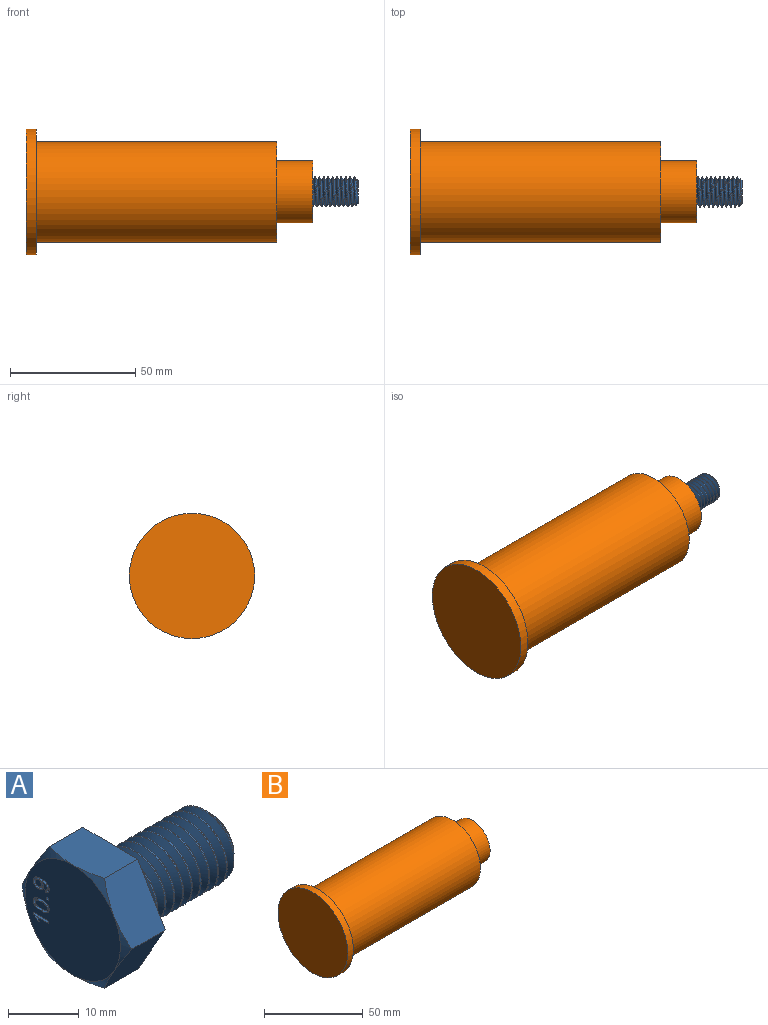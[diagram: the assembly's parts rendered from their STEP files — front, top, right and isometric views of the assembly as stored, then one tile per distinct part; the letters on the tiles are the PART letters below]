
ASSEMBLY  parts=2 mates=1
PART A: 61 faces, bbox 28.9x22.8x22.8 mm
  f0: plane 19x19mm, normal (-1,0,0), area 272.6mm2, adj f14,f15,f16,f17,f18,f19,f20,f21
  f1: plane 11.88x8.41mm, normal (0,0,-1), area 79.1mm2, adj f2,f6,f13,f16,f17
  f2: plane 10.4x8.4mm, normal (0,-0.87,-0.5), area 79.1mm2, adj f1,f3,f13,f15,f16
  f3: plane 10.4x8.4mm, normal (0,-0.87,0.5), area 79.1mm2, adj f2,f4,f13,f14,f15
  f4: plane 11.88x8.41mm, normal (0,0,1), area 79.1mm2, adj f3,f5,f13,f14,f19
  f5: plane 10.4x8.4mm, normal (0,0.87,0.5), area 79.1mm2, adj f4,f6,f13,f18,f19
  f6: plane 10.4x8.4mm, normal (0,0.87,-0.5), area 79.1mm2, adj f1,f5,f13,f17,f18
  f7: cylinder r=6mm len=18.69mm, axis (1,0,0), area 108.5mm2, adj f8,f11,f12,f13
  f8: cone r=4.69mm half-angle=45deg, axis (-1,0,0), area 34.2mm2, adj f7,f9,f10,f11,f12
  f9: plane 9.38x9.38mm, normal (1,0,0), area 69mm2, adj f8
  f10: bspline ~20.26x9.72mm, area 75.8mm2, adj f8,f11,f12,f13
  f11: bspline ~20.48x11.95mm, area 493.3mm2, adj f7,f8,f10,f13
  f12: bspline ~21.14x12mm, area 492.9mm2, adj f7,f8,f10,f13
  f13: plane 22.61x19.68mm, normal (1,0,0), area 219.4mm2, adj f1,f2,f3,f4,f5,f6,f7,f10
  f14: cone r=9.5mm half-angle=60deg, axis (1,0,0), area 8.9mm2, adj f0,f3,f4
  f15: cone r=9.5mm half-angle=60deg, axis (1,0,0), area 8.9mm2, adj f0,f2,f3
  f16: cone r=9.5mm half-angle=60deg, axis (1,0,0), area 8.9mm2, adj f0,f1,f2
  f17: cone r=9.5mm half-angle=60deg, axis (1,0,0), area 8.9mm2, adj f0,f1,f6
  f18: cone r=9.5mm half-angle=60deg, axis (1,0,0), area 8.9mm2, adj f0,f5,f6
  f19: cone r=9.5mm half-angle=60deg, axis (1,0,0), area 8.9mm2, adj f0,f4,f5
  f20: plane 3.08x0.5mm, normal (0,0,-1), area 1.5mm2, adj f0,f21,f26,f27
  f21: plane 0.5x0.4mm, normal (0,1,0), area 0.2mm2, adj f0,f20,f22,f27
  f22: plane 2.4x0.5mm, normal (0,0,1), area 1.2mm2, adj f0,f21,f23,f27
  f23: extruded ~0.71x0.5mm, area 0.4mm2, adj f0,f22,f24,f27
  f24: plane 0.5x0.36mm, normal (0,0,1), area 0.2mm2, adj f0,f23,f25,f27
  f25: extruded ~0.85x0.77mm, area 0.6mm2, adj f0,f24,f26,f27
  f26: plane 0.5x0.25mm, normal (0,-1,0), area 0.1mm2, adj f0,f20,f25,f27
  f27: plane 3.08x1.11mm, normal (-1,0,0), area 1.5mm2, adj f20,f21,f22,f23,f24,f25,f26
  f28: extruded ~1.26x0.5mm, area 0.7mm2, adj f0,f29,f32,f33
  f29: extruded ~1.56x0.99mm, area 1mm2, adj f0,f28,f30,f33
  f30: extruded ~1.56x0.99mm, area 1mm2, adj f0,f29,f31,f33
  f31: extruded ~1.56x0.99mm, area 1mm2, adj f0,f30,f32,f33
  f32: extruded ~0.69x0.5mm, area 0.4mm2, adj f0,f28,f31,f33
  f33: plane 3.12x1.98mm, normal (-1,0,0), area 2.7mm2, adj f28,f29,f30,f31,f32,f34,f35,f36
  f34: extruded ~0.99x0.5mm, area 0.5mm2, adj f33,f35,f38,f39
  f35: extruded ~0.5x0.41mm, area 0.2mm2, adj f33,f34,f36,f39
  f36: extruded ~1.21x0.6mm, area 0.8mm2, adj f33,f35,f37,f39
  f37: extruded ~1.21x0.59mm, area 0.8mm2, adj f33,f36,f38,f39
  f38: extruded ~1.21x0.59mm, area 0.8mm2, adj f33,f34,f37,f39
  f39: plane 2.41x1.19mm, normal (-1,0,0), area 2.4mm2, adj f34,f35,f36,f37,f38
  f40: plane 0.5x0.4mm, normal (0,1,0), area 0.2mm2, adj f0,f41,f43,f44
  f41: plane 0.5x0.4mm, normal (0,0,1), area 0.2mm2, adj f0,f40,f42,f44
  f42: plane 0.5x0.4mm, normal (0,-1,0), area 0.2mm2, adj f0,f41,f43,f44
  f43: plane 0.5x0.4mm, normal (0,0,-1), area 0.2mm2, adj f0,f40,f42,f44
  f44: plane 0.4x0.4mm, normal (-1,0,0), area 0.2mm2, adj f40,f41,f42,f43
  f45: extruded ~0.85x0.79mm, area 0.6mm2, adj f0,f46,f54,f55
  f46: plane 0.5x0.4mm, normal (0,-1,0.1), area 0.2mm2, adj f0,f45,f47,f55
  f47: extruded ~0.5x0.48mm, area 0.4mm2, adj f0,f46,f48,f55
  f48: extruded ~1.08x0.67mm, area 0.7mm2, adj f0,f47,f49,f55
  f49: extruded ~0.5x0.08mm, area 0mm2, adj f0,f48,f50,f55
  f50: extruded ~0.71x0.5mm, area 0.4mm2, adj f0,f49,f51,f55
  f51: extruded ~0.99x0.88mm, area 0.7mm2, adj f0,f50,f52,f55
  f52: extruded ~1.02x0.94mm, area 0.8mm2, adj f0,f51,f53,f55
  f53: extruded ~1.48x1.03mm, area 1mm2, adj f0,f52,f54,f55
  f54: extruded ~1.64x1.08mm, area 1.1mm2, adj f0,f45,f53,f55
  f55: plane 3.12x1.98mm, normal (-1,0,0), area 2.9mm2, adj f45,f46,f47,f48,f49,f50,f51,f52
  f56: extruded ~0.65x0.59mm, area 0.5mm2, adj f55,f57,f59,f60
  f57: extruded ~0.62x0.6mm, area 0.5mm2, adj f55,f56,f58,f60
  f58: extruded ~0.69x0.61mm, area 0.5mm2, adj f55,f57,f59,f60
  f59: extruded ~0.66x0.58mm, area 0.5mm2, adj f55,f56,f58,f60
  f60: plane 1.3x1.19mm, normal (-1,0,0), area 1.2mm2, adj f56,f57,f58,f59
PART B: 7 faces, bbox 114.5x50x50 mm
  f0: cylinder r=20mm len=96mm, axis (1,0,0), area 12063.7mm2, adj f1,f4
  f1: plane 50x50mm, normal (1,0,0), area 706.9mm2, adj f0,f2
  f2: cylinder r=25mm len=50mm, axis (1,0,0), area 628.3mm2, adj f1,f3
  f3: plane 50x50mm, normal (-1,0,0), area 1963.5mm2, adj f2
  f4: plane 40x40mm, normal (1,0,0), area 775.5mm2, adj f0,f5
  f5: cylinder r=12.38mm len=24.75mm, axis (-1,0,0), area 1127.4mm2, adj f4,f6
  f6: plane 24.75x24.75mm, normal (1,0,0), area 481.1mm2, adj f5
PLACE A t=(4.24,-24.82,3.7)mm
PLACE B t=(-14.51,-24.82,3.7)mm fixed
MATE revolute A.f7 <-> B.f0  axis (1,0,0) through (17.99,-24.82,3.7)mm
